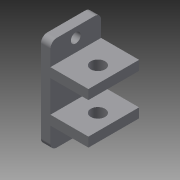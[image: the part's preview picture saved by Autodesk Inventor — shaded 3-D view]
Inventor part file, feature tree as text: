
AUTODESK INVENTOR PART (.ipt)
format: ipt  version: 2015 (Build 190159000, 159)  size: 152,064 bytes
history: native  units: in
note: dims shown in document units (in); Inventor stores cm internally (conversion verified against a paired STEP export)
features: extrude x4, sketch x2, fillet x1
ambient origin geometry x8: Origin, YZ Plane, XZ Plane, XY Plane, X Axis, Y Axis, Z Axis, Center Point
bodies: Solid1 (feature_tree)
feature tree (7):
  sketch  "Sketch1"  dims[d0=11.0236in d1=0.6693in]
  extrude  "Extrusion1"  Depth=0.6693in
  extrude  "Extrusion2"  Depth=0.3937in
  extrude  "Extrusion3"  Depth=0.0787in
  extrude  "Extrusion4"  Depth=0.0787in
  fillet  "Fillet1"  Radius=2.7559in
  sketch  "Sketch2"  dims[d2=11.0236in d3=0.3937in d4=1.5748in d5=4.9213in d6=2.7559in d7=0.7874in d8=0.7874in d10=0.9843in d11=0.126in d12=0.4724in d13=0.4724in d14=0.315in d16=0.1181in d17=0.2362in d18=0.189in d19=0.4724in d20=0.4724in d21=0.1181in d22=0.2756in d23=0.1772in d24=0.1969in d25=0.315in d26=0.315in d27=0.6299in d28=0.0in d29=0.3937in d30=0.0in d31=1.1811in d32=0.0in d33=0.315in d34=0.1181in d35=0.122in d36=0.315in d37=0.1181in d38=0.122in d39=1.1811in d40=0.0in d41=0.0787in]
